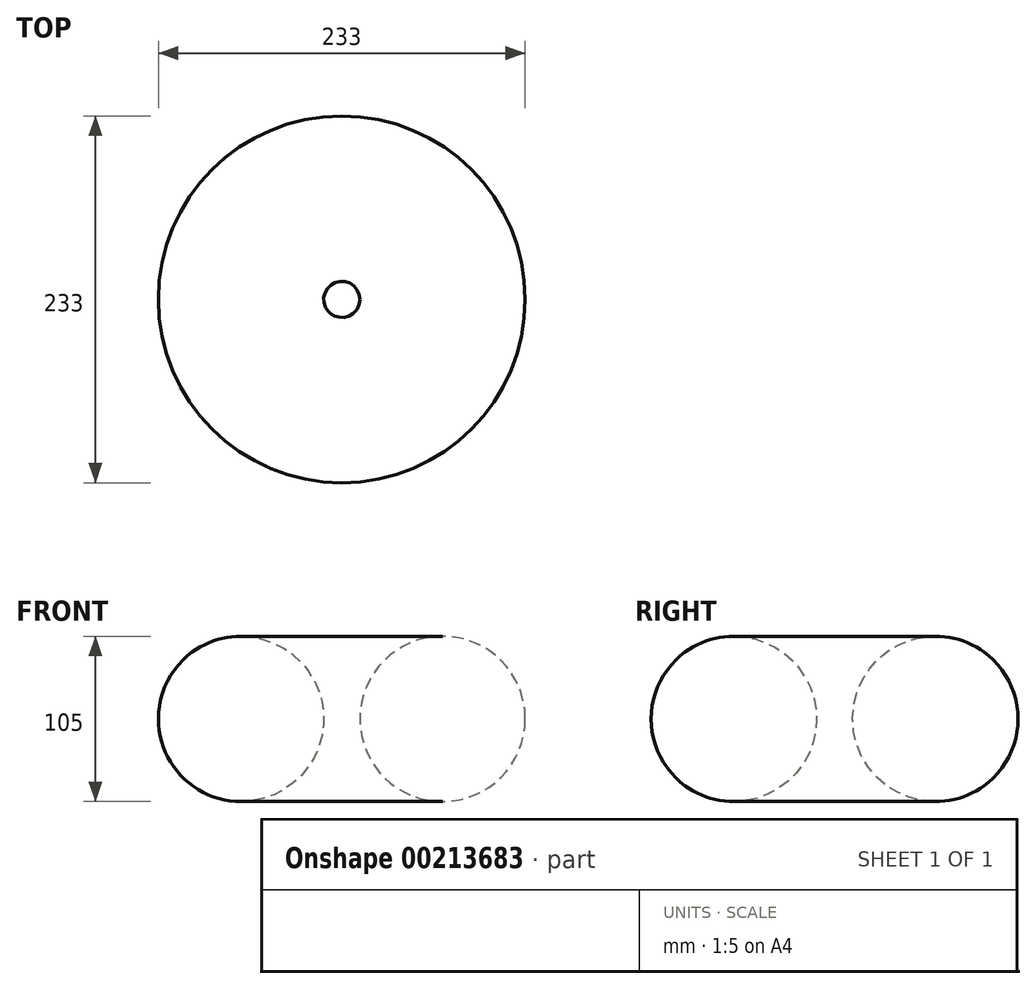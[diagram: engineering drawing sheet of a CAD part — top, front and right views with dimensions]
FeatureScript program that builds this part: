
annotation { "Feature Type Name" : "Feature", "Feature Type Description" : "" }
export const myFeature = defineFeature(function(context is Context, id is Id, definition is map)
    precondition{}
    {
        {
            var Q0;
            Q0=qCreatedBy(makeId("Front.planeOp"),FACE);
            var sketch = newSketch(context, id + "F0", { "sketchPlane" : qUnion([Q0])});
            skCircle(sketch, "E0", {"center": v(-64, 0) * mm, "radius": 52.5 * mm});
            skLineSegment(sketch, "E1", {"start": v(0, 0) * mm, "end": v(0, 96) * mm, "construction": true});
            skSolve(sketch);
        }
        {
            var Q0;
            Q0=sQuery(id+"F0.wireOp",EDGE,"E0");
            var Q1;
            Q1=sQuery(id+"F0.wireOp",EDGE,"E1");
            revolve(context, id + "F1", {"bodyType" : ToolBodyType.SURFACE, "surfaceEntities" : qUnion([Q0]), "axis" : qUnion([Q1]), "revolveType" : RevolveType.FULL});
        }
    });
